# Revit family: Gira_129000
name_source: partatom
category: Elektroinstallationen
revit_build: Autodesk Revit 2017 (Build: 20160225_1515(x64)
units: mm (PartAtom-declared; Revit-internal decimal feet)

## family parameters
Basisbauteil = Fläche
Beim Laden mit Abzugskörper schneiden = Nein
Bemaßung runder Anschluss = Durchmesser verwenden
Beschriftungsausrichtung beibehalten = Nein
Gemeinsam genutzt = Nein
Raumberechnungspunkt = Nein
Teiletyp = Normal

## types (1)
- TKS-TK-Gateway REG Türko
    BIM = https://media.live.bim.site 00_REG 6.rfa
    BIMSITE_PRODUCT_ID = 66ffb45fde7ee73d94dea6cf34e9c73e25d05be4
    Beschreibung = TKS-TK-Gateway  REG Merkmale:  TKS-TK-Gateway zur Verbindung des Gira Türkommunikations-Systems mit der vorhandenen Telefonanlage.  Bei einem analogen Telefonanschluss wird das TKS-TK-Gateway einfach zwischen Telefonanschluss und analogem Telefon geschaltet. Telefongespräche können, wie gewohnt, am vorhandenen Telefon geführt werden.  Zusätzlich werden Türrufe vom Gira Türkommunikations-System zum Telefon weitergeleitet, es kann mit der Person an der Haustür gesprochen und der Türöffner über die Telefontastatur aktiviert werden.  Außerdem können Türrufe an einen Anrufbeantworter oder ein Mobiltelefon weitergeleitet werden.  Annahme von Türrufen über das vorhandene Telefon.  Direkter Amtsanschluss, bei Analogbetrieb keine TK-Anlage erforderlich.  Anschlussmöglichkeit an den a b-Anschluss vorhandener TK-Anlagen.  Rufweiterleitung an Lokal-, Festnetz oder Mobiltelefon.  Rufweiterleitung an bis zu 50 programmierte Teilnehmer.  Rufunterscheidung zwischen Amtsanruf und Türruf.  Umschaltmöglichkeit zwischen Tag- und Nachtbetrieb.  Unterstützung der Anklopffunktion bei einem vorhandenen Amtsgespräch und einem eingehenden Türruf.  Konfigurierbar über Tastatur des Telefons (DTMF-fähig) oder das Programmierset.  Ruf und Gesprächsdauer einstellbar.  Mithörsperre.  Betrieb von mehreren TKS-TK-Gateways am Gira Türkommunikationsbus möglich.   Durchführung von Schaltfunktionen über das vorhandene Telefon (DTMF-fähig) in Kombination mit dem Schaltaktor oder dem Unterputz-Schaltaktor.  LED-Statusanzeigen, zur schnellen Analyse, ob Netzspannung anliegt und der Telefonanschluss belegt wurde.  Verpolungssichere Anschlüsse.  Programmierschnittstelle und integrierter Flash-Prozessor zur Aktualisierung der TKS-TK-Gateway Software.  Mit dieser Komponente ist der Aufbau von Türkommunikationsanlagen mit mehr als 30 Teilnehmern möglich. Die Spannungsversorgung des TKS-TK-Gateways erfolgt über:  den 12-V-Ausgang des Steuergeräts Audio.  einen handelsüblichen AC 12 V Klingeltransformator bei Verwendung des Steuergerätes Video).  die Spannungsversorung für Türkommunikation DC 24 V (bei Verwendung des Steuergerätes Video).  Hinweise :  Konfigurationsänderungen über Telefon erfolgen aus Sicherheitsgründen erst nach Eingabe eines 4-stelligen PIN-Codes.  Beim Betrieb mehrerer TKS-TK-Gateways in einer Anlage muss jedes TKS-TK-Gateway über eine eigene Spannungsversorgung verfügen. Die Versorgung mehrerer TKS-TK-Gateways aus einem Steuergerät oder aus einem Klingeltransformator ist nicht zulässig.  Das TKS-TK-Gateway ist für den Einbau in die Unterverteilung vorgesehen. Ist dies nicht möglich, handelsüblichen Aufputzverteiler verwenden.
    Datenblatt = https://media.live.bim.site
    Datenblatt 1 = https://media.live.bim.site
    Funktion = steuern/regeln
    GTIN = 4010337290001
    HAN = 129000
    HeinzeBIM = https://www.heinze.de
    Hersteller = Gira
    Installationstechnik = Bus-System
    Ist System = Nein
    Ist Zubehör = Nein
    Kosten = 0 $
    Produktseite = https://media.live.bim.site
    Typname = TKS-TK-Gateway REG Türko
    URL = https://www.gira.de
    Vorgabe-Ansicht = 1219 mm

## geometry (parser evidence)
native form markers: Sweep x2
no freeform markers — native parametric forms only
